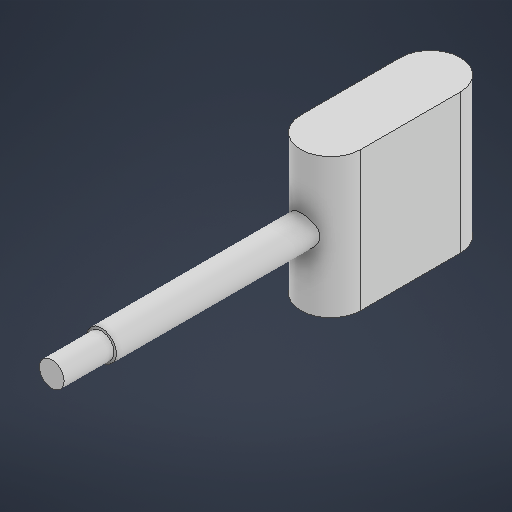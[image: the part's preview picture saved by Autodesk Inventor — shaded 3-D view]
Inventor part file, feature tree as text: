
AUTODESK INVENTOR PART (.ipt)
format: ipt  version: 2025.3 (Build 293356000, 356)  size: 212,480 bytes
history: native  units: mm
features: extrude x3, sketch x3, plane x1
ambient origin geometry x8: Origin, YZ Plane, XZ Plane, XY Plane, X Axis, Y Axis, Z Axis, Center Point
bodies: Solid1 (feature_tree)
feature tree (7):
  extrude  "Extrusion1"  Depth=3.0mm
  plane  "Work Plane1"
  extrude  "Extrusion2"  Depth=14.0mm TaperAngle=0.0deg
  extrude  "Extrusion3"  Depth=5.0mm
  sketch  "Sketch1"  dims[d0=10.0mm d1=3.0mm]
  sketch  "Sketch2"  dims[d2=20.0mm d3=14.0mm d4=0.0mm]
  sketch  "Sketch3"  dims[d5=3.0mm d6=7.0mm d7=3.0mm d8=25.0mm d9=2.0mm d10=0.0mm d11=0.0mm d12=2.5mm d13=5.0mm d14=0.0mm]
